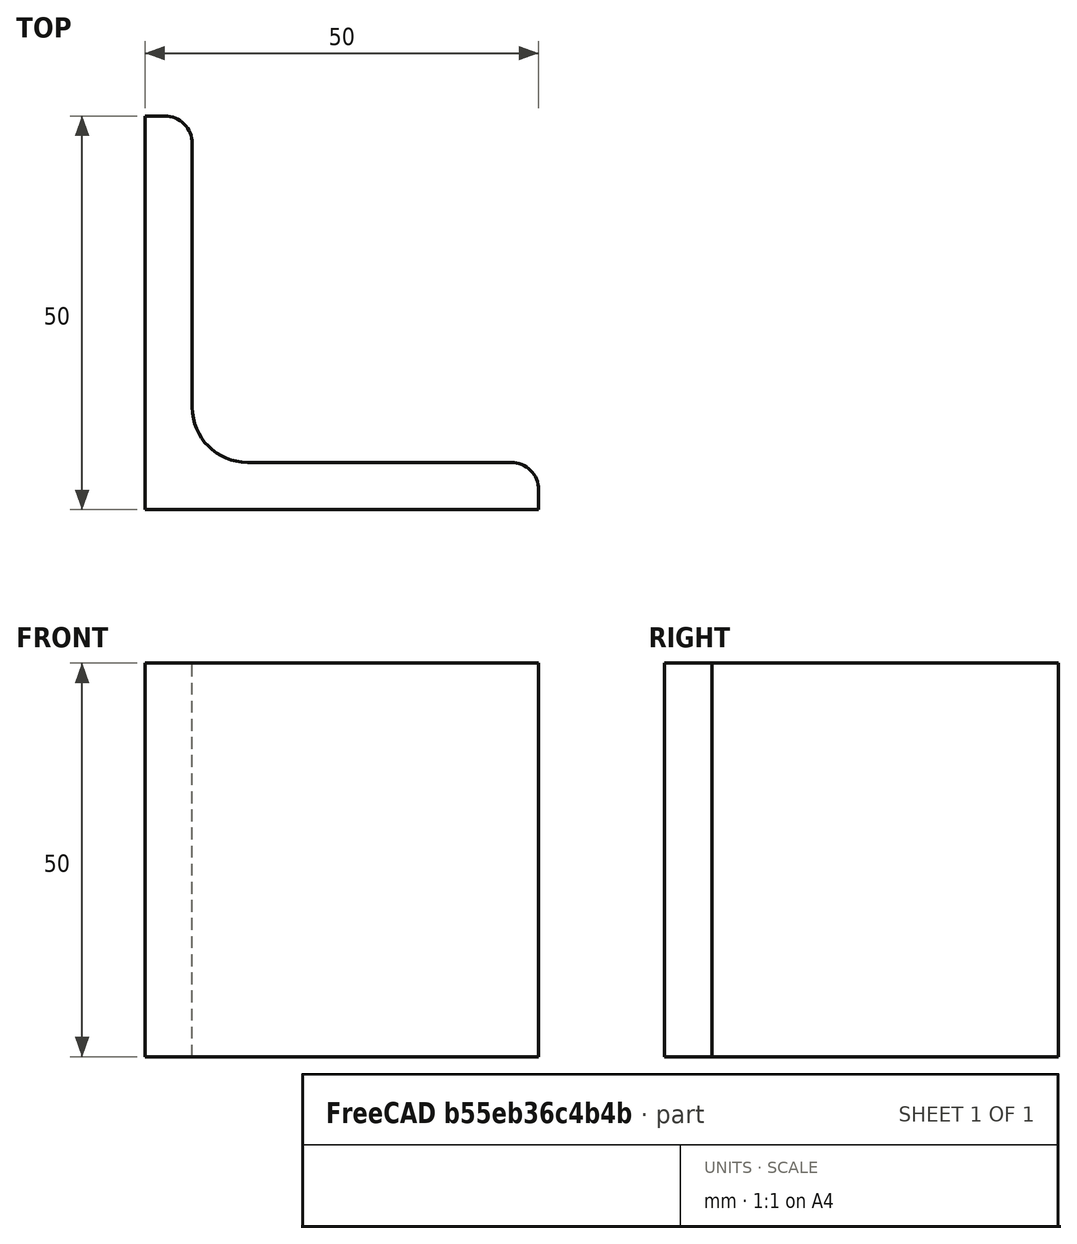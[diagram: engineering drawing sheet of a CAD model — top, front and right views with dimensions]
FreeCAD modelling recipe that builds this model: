
FCSTD DOCUMENT  (FreeCAD 0.15R4671 (Git))
Label: Angle Bar L50x50x6 EN10056 S235JR
License: All rights reserved
LicenseURL: http://en.wikipedia.org/wiki/All_rights_reserved
objects: Sketcher::SketchObject×1, Part::Extrusion×1
note: 2 computed .brp shape members not serialized (recipe doc carries the construction recipe); baked Part::Feature solids carry a one-line shape summary decoded from their .brp

FEATURE [Sketcher::SketchObject] Sketch
  sketch-geometry (9):
    g0: LineSegment StartX=0 StartY=0 StartZ=0 EndX=50 EndY=0 EndZ=0
    g1: LineSegment StartX=50 StartY=0 StartZ=0 EndX=50 EndY=2.5 EndZ=0
    g2: LineSegment StartX=46.5 StartY=6 StartZ=0 EndX=13 EndY=6 EndZ=0
    g3: LineSegment StartX=0 StartY=0 StartZ=0 EndX=0 EndY=50 EndZ=0
    g4: LineSegment StartX=0 StartY=50 StartZ=0 EndX=2.5 EndY=50 EndZ=0
    g5: LineSegment StartX=6 StartY=46.5 StartZ=0 EndX=6 EndY=13 EndZ=0
    g6: ArcOfCircle CenterX=13 CenterY=13 CenterZ=0 NormalX=0 NormalY=0 NormalZ=1 Radius=7 StartAngle=3.14159 EndAngle=4.71239
    g7: ArcOfCircle CenterX=2.5 CenterY=46.5 CenterZ=0 NormalX=0 NormalY=0 NormalZ=1 Radius=3.5 StartAngle=0 EndAngle=1.5708
    g8: ArcOfCircle CenterX=46.5 CenterY=2.5 CenterZ=0 NormalX=0 NormalY=0 NormalZ=1 Radius=3.5 StartAngle=0 EndAngle=1.5708
  constraints (23):
    c: Coincident(g0,g-1)
    c: Horizontal(g0)
    c: Coincident(g1,g0)
    c: Vertical(g1)
    c: Horizontal(g2)
    c: Coincident(g3,g-1)
    c: Vertical(g3)
    c: Coincident(g4,g3)
    c: Horizontal(g4)
    c: Vertical(g5)
    c: Tangent(g5,g6) = -1.5708
    c: Tangent(g2,g6) = 1.5708
    c: Tangent(g4,g7) = 1.5708
    c: Tangent(g5,g7) = 1.5708
    c: Tangent(g2,g8) = -1.5708
    c: Tangent(g1,g8) = -1.5708
    c: DistanceX(g0) = 50
    c: DistanceY(g3) = 50
    c: DistanceY(g0,g2) = 6
    c: DistanceX(g3,g5) = 6
    c: Radius(g6) = 7
    c: Radius(g8) = 3.5
    c: Radius(g7) = 3.5
FEATURE [Part::Extrusion] Extrude  label="Angle Bar L50x50x6 EN10056 S235JR"
  Base = -> Sketch
  Dir = (0,0,50)
  Solid = true
